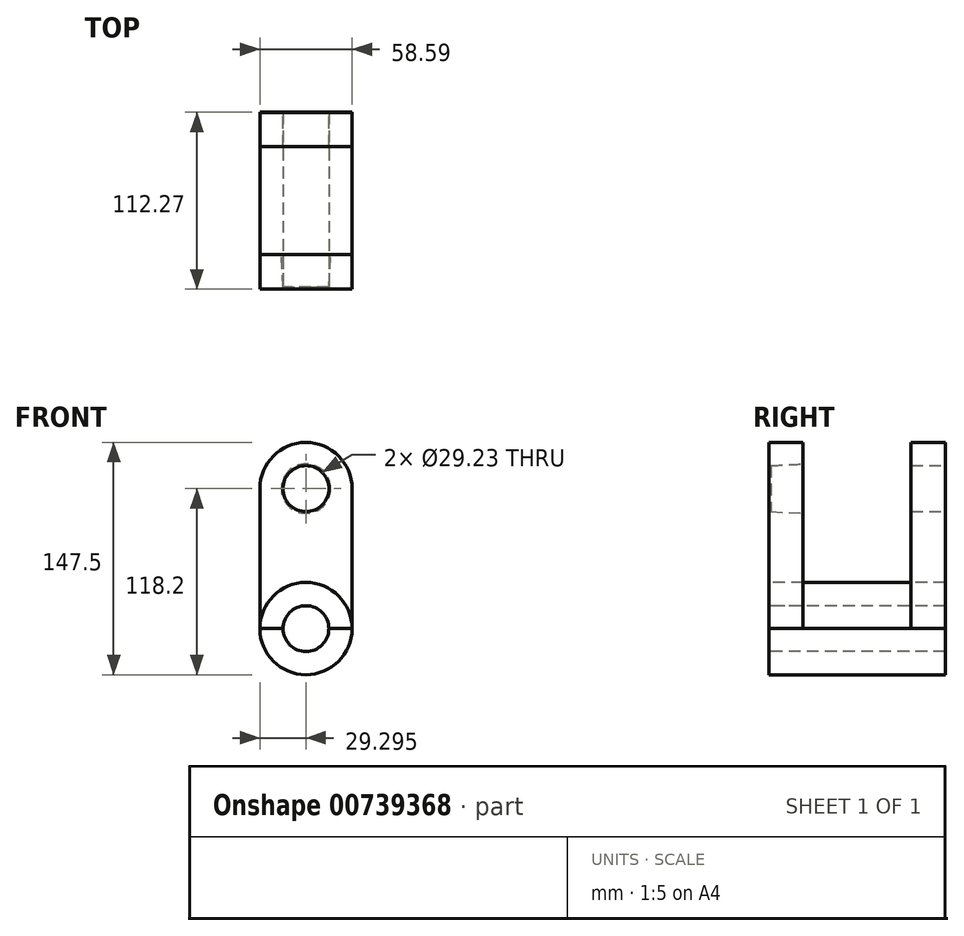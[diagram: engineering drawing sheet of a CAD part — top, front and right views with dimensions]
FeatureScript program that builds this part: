
annotation { "Feature Type Name" : "Feature", "Feature Type Description" : "" }
export const myFeature = defineFeature(function(context is Context, id is Id, definition is map)
    precondition{}
    {
        {
            var Q0;
            Q0=qCreatedBy(makeId("Top.planeOp"),FACE);
            var sketch = newSketch(context, id + "F0", { "sketchPlane" : qUnion([Q0])});
            skLineSegment(sketch, "E0.bottom", {"start": v(-28.31, -34.43) * mm, "end": v(30.28, -34.43) * mm});
            skLineSegment(sketch, "E0.top", {"start": v(-28.31, -56.23) * mm, "end": v(30.28, -56.23) * mm});
            skLineSegment(sketch, "E0.left", {"start": v(-28.31, -34.43) * mm, "end": v(-28.31, -56.23) * mm});
            skLineSegment(sketch, "E0.right", {"start": v(30.28, -34.43) * mm, "end": v(30.28, -56.23) * mm});
            skLineSegment(sketch, "E1.bottom", {"start": v(-28.31, 55.98) * mm, "end": v(30.28, 55.98) * mm});
            skLineSegment(sketch, "E1.top", {"start": v(-28.31, 34.18) * mm, "end": v(30.28, 34.18) * mm});
            skLineSegment(sketch, "E1.left", {"start": v(-28.31, 55.98) * mm, "end": v(-28.31, 34.18) * mm});
            skLineSegment(sketch, "E1.right", {"start": v(30.28, 55.98) * mm, "end": v(30.28, 34.18) * mm});
            skPoint(sketch, "E2", {"position": v(-28.31, -34.43) * mm});
            skSolve(sketch);
        }
        {
            var Q0;
            Q0=makeQuery(id+"F0.imprint","IMPRINT",FACE,{"disambiguationData":[TD([[makeQuery(id+"F0.imprint","IMPRINT",EDGE,{"derivedFrom":sQuery(id+"F0.wireOp",EDGE,"E0.bottom")}),-1.0]])]});
            var Q1;
            Q1=makeQuery(id+"F0.imprint","IMPRINT",FACE,{"disambiguationData":[TD([[makeQuery(id+"F0.imprint","IMPRINT",EDGE,{"derivedFrom":sQuery(id+"F0.wireOp",EDGE,"E1.bottom")}),-1.0]])]});
            extrude(context, id + "F1", {"entities" : qUnion([Q0, Q1]), "depth" : 88.9 * mm, "offsetDistance" : 25.4 * mm});
        }
        {
            var Q0;
            Q0=makeQuery(id+"F1.opExtrude","SWEPT_FACE",FACE,{"disambiguationData":[OSD([sQuery(id+"F0.wireOp",EDGE,"E0.top")])]});
            var sketch = newSketch(context, id + "F2", { "sketchPlane" : qUnion([Q0])});
            skCircle(sketch, "E3", {"center": v(0.99, 0) * mm, "radius": 29.3 * mm});
            skPoint(sketch, "E3.first.point", {"position": v(-28.31, 0) * mm});
            skPoint(sketch, "E3.second.point", {"position": v(30.28, 0) * mm});
            skPoint(sketch, "E3.third.point", {"position": v(14.64, -25.92) * mm});
            skCircle(sketch, "E4", {"center": v(0.99, 0) * mm, "radius": 14.55 * mm});
            skSolve(sketch);
        }
        {
            var Q0;
            {var subQ1=sQuery(id+"F0.wireOp",EDGE,"E0.top");Q0=makeQuery(id+"F2.imprint","IMPRINT",FACE,{"disambiguationData":[TD([[makeQuery(id+"F2.imprint","IMPRINT",EDGE,{"derivedFrom":makeQuery(id+"F1.opExtrude","CAP_EDGE",EDGE,{"disambiguationData":[OSD([subQ1])],"isStart":false})}),-1.0]])]});}
            var sketch = newSketch(context, id + "F3", { "sketchPlane" : qUnion([Q0])});
            skPoint(sketch, "E5", {"position": v(-28.31, 88.9) * mm});
            skPoint(sketch, "E6", {"position": v(30.28, 88.9) * mm});
            skSolve(sketch);
        }
        {
            var Q0;
            {var subQ1=sQuery(id+"F0.wireOp",EDGE,"E0.top");Q0=makeQuery(id+"F2.imprint","IMPRINT",FACE,{"disambiguationData":[TD([[makeQuery(id+"F2.imprint","IMPRINT",EDGE,{"derivedFrom":makeQuery(id+"F1.opExtrude","CAP_EDGE",EDGE,{"disambiguationData":[OSD([subQ1])],"isStart":false})}),-1.0]])]});}
            var sketch = newSketch(context, id + "F4", { "sketchPlane" : qUnion([Q0])});
            skCircle(sketch, "E7", {"center": v(0.99, 88.9) * mm, "radius": 29.3 * mm});
            skPoint(sketch, "E7.first.point", {"position": v(30.28, 88.9) * mm});
            skPoint(sketch, "E7.second.point", {"position": v(-28.31, 88.9) * mm});
            skPoint(sketch, "E7.third.point", {"position": v(0, 59.62) * mm});
            skCircle(sketch, "E8", {"center": v(0.99, 88.9) * mm, "radius": 14.55 * mm});
            skSolve(sketch);
        }
        {
            var Q0;
            {var subQ0=sQuery(id+"F4.wireOp",EDGE,"E8");var subQ1=makeQuery(id+"F2.imprint","IMPRINT",EDGE,{"derivedFrom":makeQuery(id+"F1.opExtrude","CAP_EDGE",EDGE,{"disambiguationData":[OSD([sQuery(id+"F0.wireOp",EDGE,"E0.top")])],"isStart":false})});var subQ2=makeQuery(id+"F4.imprint","INTERSECT",VERTEX,{"disambiguationData":[OD(0.0)],"derivedFrom":[subQ1,subQ0]});Q0=makeQuery(id+"F4.imprint","IMPRINT",FACE,{"disambiguationData":[TD([[makeQuery(id+"F4.imprint","IMPRINT",EDGE,{"disambiguationData":[TD([[subQ2,-1.0]])],"derivedFrom":subQ0}),1.0]])]});}
            extrude(context, id + "F5", {"entities" : qUnion([Q0]), "operationType" : NewBodyOperationType.REMOVE, "oppositeDirection" : true, "depth" : 127 * mm, "offsetDistance" : 25.4 * mm});
        }
        {
            var Q0;
            {var subQ1=sQuery(id+"F0.wireOp",EDGE,"E0.top");var subQ2=makeQuery(id+"F2.imprint","IMPRINT",EDGE,{"derivedFrom":makeQuery(id+"F1.opExtrude","CAP_EDGE",EDGE,{"disambiguationData":[OSD([subQ1])],"isStart":false})});var subQ5=sQuery(id+"F4.wireOp",EDGE,"E8");var subQ6=makeQuery(id+"F4.imprint","INTERSECT",VERTEX,{"disambiguationData":[OD(0.0)],"derivedFrom":[subQ2,subQ5]});Q0=makeQuery(id+"F4.imprint","IMPRINT",FACE,{"disambiguationData":[TD([[makeQuery(id+"F4.imprint","IMPRINT",EDGE,{"disambiguationData":[TD([[subQ6,1.0]])],"derivedFrom":subQ5}),-1.0]])]});}
            extrude(context, id + "F6", {"entities" : qUnion([Q0]), "operationType" : NewBodyOperationType.ADD, "oppositeDirection" : true, "depth" : 112.22 * mm, "offsetDistance" : 25.4 * mm});
        }
        {
            var Q0;
            {var subQ1=sQuery(id+"F0.wireOp",EDGE,"E0.top");var subQ2=makeQuery(id+"F1.opExtrude","CAP_EDGE",EDGE,{"disambiguationData":[OSD([subQ1])],"isStart":true});var subQ5=sQuery(id+"F2.wireOp",EDGE,"E4");var subQ6=makeQuery(id+"F2.imprint","INTERSECT",VERTEX,{"disambiguationData":[OD(0.0)],"derivedFrom":[subQ2,subQ5]});Q0=makeQuery(id+"F2.imprint","IMPRINT",FACE,{"disambiguationData":[TD([[makeQuery(id+"F2.imprint","IMPRINT",EDGE,{"disambiguationData":[TD([[subQ6,1.0]])],"derivedFrom":subQ5}),-1.0]])]});}
            extrude(context, id + "F7", {"entities" : qUnion([Q0]), "oppositeDirection" : true, "depth" : 112.27 * mm, "offsetDistance" : 25.4 * mm});
        }
        {
            var Q0;
            {var subQ1=sQuery(id+"F0.wireOp",EDGE,"E0.top");var subQ2=makeQuery(id+"F1.opExtrude","CAP_EDGE",EDGE,{"disambiguationData":[OSD([subQ1])],"isStart":true});var subQ5=sQuery(id+"F2.wireOp",EDGE,"E4");var subQ6=makeQuery(id+"F2.imprint","INTERSECT",VERTEX,{"disambiguationData":[OD(0.0)],"derivedFrom":[subQ2,subQ5]});Q0=makeQuery(id+"F2.imprint","IMPRINT",FACE,{"disambiguationData":[TD([[makeQuery(id+"F2.imprint","IMPRINT",EDGE,{"disambiguationData":[TD([[subQ6,-1.0]])],"derivedFrom":subQ5}),-1.0]])]});}
            extrude(context, id + "F8", {"entities" : qUnion([Q0]), "oppositeDirection" : true, "depth" : 112.22 * mm, "offsetDistance" : 25.4 * mm});
        }
        {
            var Q0;
            {var subQ0=sQuery(id+"F2.wireOp",EDGE,"E4");var subQ1=makeQuery(id+"F1.opExtrude","CAP_EDGE",EDGE,{"disambiguationData":[OSD([sQuery(id+"F0.wireOp",EDGE,"E0.top")])],"isStart":true});var subQ2=makeQuery(id+"F2.imprint","INTERSECT",VERTEX,{"disambiguationData":[OD(0.0)],"derivedFrom":[subQ1,subQ0]});Q0=makeQuery(id+"F2.imprint","IMPRINT",FACE,{"disambiguationData":[TD([[makeQuery(id+"F2.imprint","IMPRINT",EDGE,{"disambiguationData":[TD([[subQ2,1.0]])],"derivedFrom":subQ0}),1.0]])]});}
            extrude(context, id + "F9", {"entities" : qUnion([Q0]), "operationType" : NewBodyOperationType.REMOVE, "oppositeDirection" : true, "depth" : 127 * mm, "offsetDistance" : 25.4 * mm});
        }
        {
            var Q0;
            Q0=makeQuery(id+"F1.opExtrude","SWEPT_FACE",FACE,{"disambiguationData":[OSD([sQuery(id+"F0.wireOp",EDGE,"E1.bottom")])]});
            var sketch = newSketch(context, id + "F10", { "sketchPlane" : qUnion([Q0])});
            skCircle(sketch, "E9", {"center": v(-0.99, 88.9) * mm, "radius": 14.62 * mm});
            skSolve(sketch);
        }
        {
            var Q0;
            {var subQ0=sQuery(id+"F10.wireOp",EDGE,"E9");var subQ1=makeQuery(id+"F1.opExtrude","CAP_EDGE",EDGE,{"disambiguationData":[OSD([sQuery(id+"F0.wireOp",EDGE,"E1.bottom")])],"isStart":false});var subQ2=makeQuery(id+"F10.imprint","INTERSECT",VERTEX,{"disambiguationData":[OD(0.0)],"derivedFrom":[subQ1,subQ0]});Q0=makeQuery(id+"F10.imprint","IMPRINT",FACE,{"disambiguationData":[TD([[makeQuery(id+"F10.imprint","IMPRINT",EDGE,{"disambiguationData":[TD([[subQ2,1.0]])],"derivedFrom":subQ0}),1.0]])]});}
            extrude(context, id + "F11", {"entities" : qUnion([Q0]), "operationType" : NewBodyOperationType.REMOVE, "oppositeDirection" : true, "depth" : 127 * mm, "offsetDistance" : 25.4 * mm});
        }
        {
            var Q0;
            Q0=makeQuery(id+"F1.opExtrude","SWEPT_FACE",FACE,{"disambiguationData":[OSD([sQuery(id+"F0.wireOp",EDGE,"E1.bottom")])]});
            var sketch = newSketch(context, id + "F12", { "sketchPlane" : qUnion([Q0])});
            skCircle(sketch, "E10", {"center": v(-0.99, 0) * mm, "radius": 14.4 * mm});
            skSolve(sketch);
        }
        {
            var Q0;
            {var subQ0=sQuery(id+"F12.wireOp",EDGE,"E10");var subQ1=makeQuery(id+"F1.opExtrude","CAP_EDGE",EDGE,{"disambiguationData":[OSD([sQuery(id+"F0.wireOp",EDGE,"E1.bottom")])],"isStart":true});var subQ2=makeQuery(id+"F12.imprint","INTERSECT",VERTEX,{"disambiguationData":[OD(0.0)],"derivedFrom":[subQ1,subQ0]});Q0=makeQuery(id+"F12.imprint","IMPRINT",FACE,{"disambiguationData":[TD([[makeQuery(id+"F12.imprint","IMPRINT",EDGE,{"disambiguationData":[TD([[subQ2,-1.0]])],"derivedFrom":subQ0}),1.0]])]});}
            extrude(context, id + "F13", {"entities" : qUnion([Q0]), "operationType" : NewBodyOperationType.REMOVE, "oppositeDirection" : true, "depth" : 50.8 * mm, "offsetDistance" : 25.4 * mm});
        }
        {
            var Q0;
            Q0=makeQuery(id+"F1.opExtrude","SWEPT_FACE",FACE,{"disambiguationData":[OSD([sQuery(id+"F0.wireOp",EDGE,"E0.right")])]});
            var sketch = newSketch(context, id + "F14", { "sketchPlane" : qUnion([Q0])});
            skLineSegment(sketch, "E11.bottom", {"start": v(-34.43, 88.9) * mm, "end": v(34.18, 88.9) * mm});
            skLineSegment(sketch, "E11.top", {"start": v(-34.43, 121.16) * mm, "end": v(34.18, 121.16) * mm});
            skLineSegment(sketch, "E11.left", {"start": v(-34.43, 88.9) * mm, "end": v(-34.43, 121.16) * mm});
            skLineSegment(sketch, "E11.right", {"start": v(34.18, 88.9) * mm, "end": v(34.18, 121.16) * mm});
            skSolve(sketch);
        }
        {
            var Q0;
            Q0=makeQuery(id+"F14.imprint","IMPRINT",FACE,{"disambiguationData":[TD([[makeQuery(id+"F14.imprint","IMPRINT",EDGE,{"derivedFrom":sQuery(id+"F14.wireOp",EDGE,"E11.bottom")}),1.0]])]});
            extrude(context, id + "F15", {"entities" : qUnion([Q0]), "operationType" : NewBodyOperationType.REMOVE, "oppositeDirection" : true, "depth" : 76.2 * mm, "offsetDistance" : 25.4 * mm});
        }
        {
            var Q0;
            {var subQ0=sQuery(id+"F4.wireOp",EDGE,"E8");var subQ1=makeQuery(id+"F2.imprint","IMPRINT",EDGE,{"derivedFrom":makeQuery(id+"F1.opExtrude","CAP_EDGE",EDGE,{"disambiguationData":[OSD([sQuery(id+"F0.wireOp",EDGE,"E0.top")])],"isStart":false})});var subQ2=makeQuery(id+"F4.imprint","INTERSECT",VERTEX,{"disambiguationData":[OD(0.0)],"derivedFrom":[subQ1,subQ0]});Q0=makeQuery(id+"F4.imprint","IMPRINT",FACE,{"disambiguationData":[TD([[makeQuery(id+"F4.imprint","IMPRINT",EDGE,{"disambiguationData":[TD([[subQ2,1.0]])],"derivedFrom":subQ0}),1.0]])]});}
            var sketch = newSketch(context, id + "F16", { "sketchPlane" : qUnion([Q0])});
            skCircle(sketch, "E12", {"center": v(0.99, 88.9) * mm, "radius": 14.55 * mm});
            skSolve(sketch);
        }
        {
            var Q0;
            {var subQ1=sQuery(id+"F4.wireOp",EDGE,"E8");var subQ2=makeQuery(id+"F2.imprint","IMPRINT",EDGE,{"derivedFrom":makeQuery(id+"F1.opExtrude","CAP_EDGE",EDGE,{"disambiguationData":[OSD([sQuery(id+"F0.wireOp",EDGE,"E0.top")])],"isStart":false})});var subQ3=makeQuery(id+"F4.imprint","IMPRINT",EDGE,{"disambiguationData":[TD([[makeQuery(id+"F4.imprint","INTERSECT",VERTEX,{"disambiguationData":[OD(0.0)],"derivedFrom":[subQ2,subQ1]}),-1.0]])],"derivedFrom":subQ2});Q0=makeQuery(id+"F16.imprint","IMPRINT",FACE,{"disambiguationData":[TD([[makeQuery(id+"F16.imprint","IMPRINT",EDGE,{"derivedFrom":subQ3}),-1.0]])]});}
            var Q1;
            {var subQ1=sQuery(id+"F4.wireOp",EDGE,"E8");var subQ2=makeQuery(id+"F2.imprint","IMPRINT",EDGE,{"derivedFrom":makeQuery(id+"F1.opExtrude","CAP_EDGE",EDGE,{"disambiguationData":[OSD([sQuery(id+"F0.wireOp",EDGE,"E0.top")])],"isStart":false})});var subQ3=makeQuery(id+"F4.imprint","IMPRINT",EDGE,{"disambiguationData":[TD([[makeQuery(id+"F4.imprint","INTERSECT",VERTEX,{"disambiguationData":[OD(0.0)],"derivedFrom":[subQ2,subQ1]}),-1.0]])],"derivedFrom":subQ2});Q1=makeQuery(id+"F16.imprint","IMPRINT",FACE,{"disambiguationData":[TD([[makeQuery(id+"F16.imprint","IMPRINT",EDGE,{"derivedFrom":subQ3}),1.0]])]});}
            extrude(context, id + "F17", {"entities" : qUnion([Q0, Q1]), "operationType" : NewBodyOperationType.REMOVE, "oppositeDirection" : true, "depth" : 44.96 * mm, "offsetDistance" : 25.4 * mm, "hasDraft" : true, "draftAngle" : 3 * degree});
        }
    });
